# Revit family: Begleitplatte
name_source: partatom
category: Allgemeines Modell
revit_build: Autodesk Revit 2016 (Build: 20161004_0715(x64)
units: mm (PartAtom-declared; Revit-internal decimal feet)

## family parameters
Arbeitsebenenbasiert = Nein
Beim Laden mit Abzugskörper schneiden = Nein
Bemaßung runder Anschluss = Durchmesser verwenden
Gemeinsam genutzt = Nein
Immer vertikal = Ja
Kann Basisbauteil für Bewehrung sein = Nein
Raumberechnungspunkt = Nein
Teiletyp = Normal

## types (6) — shared parameters
Auftrittsfläche = Rändelstruktur
Fasenausbildung = Minifase
Material = Hochleistungsfaserbeton
Produktfamilie = Begleitplatte
Produktionsnorm = DIN V 18500
Produzent = IKM Betonsteinwerk Knapp & Co GmbH, Muggensturm
Rastermaß L/ B in mm = 300/300
www = www.Betonsteinwerk-Knapp.de

## per-type parameters (varying)
| type | 64.5 | 80.45 | Artikelnummer | Farbausführung | GTIN - Nummer | Gewicht/St | LRV-Wert | Materialität | Produktname | R-Wert  nach DIN 51130 |
| Sicherungselement "Strich" - 300/300/64,5 Weiß | Ja | Nein | 5-303108-470-00 | Nr. 470 Weiß | 4060851017097 | 12.2 | 53,06 | Nr. 470 Weiß | Sicherungselement "Strich" | R12 |
| Sicherungselement "Strich" - 300/300/80,45 Weiß | Nein | Ja | 5-303108-470-00 | Nr. 470 Weiß | 4060851017097 | 16,6 | 53,06 | Nr. 470 Weiß | Sicherungselement "Strich" | R12 |
| Begleitplatte - 300/300/80,45 Anthrazit | Nein | Ja | 5-393008-469-90 | Nr. 469 Anthrazit mit Oberflächenvergütung | 4060851017080 | 16,6 |  | Nr. 469 Anthrazit | Begleitplatte | R11 |
| Begleitplatte - 300/300/64,5 Anthrazit | Ja | Nein | 5-393008-469-90 | Nr. 469 Anthrazit mit Oberflächenvergütung | 4060851017080 | 12.2 |  | Nr. 469 Anthrazit | Begleitplatte | R11 |
| Sicherungselement "Strich" - 300/300/80,45 Anthrazit | Nein | Ja | 5-303108-469-90 | Nr. 469 Anthrazit mit Oberflächenvergütung | 4060851017103 | 16,6 |  | Nr. 469 Anthrazit | Sicherungselement "Strich" | R11 |
| Sicherungselement "Strich" - 300/300/64,5 Anthrazit | Ja | Nein | 5-303108-469-90 | Nr. 469 Anthrazit mit Oberflächenvergütung | 4060851017103 | 12.2 |  | Nr. 469 Anthrazit | Sicherungselement "Strich" | R12 |
